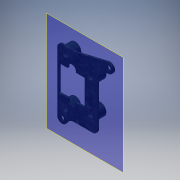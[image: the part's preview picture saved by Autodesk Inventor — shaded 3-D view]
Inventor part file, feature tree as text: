
AUTODESK INVENTOR PART (.ipt)
format: ipt  version: 2017 (Build 210142000, 142)  size: 265,216 bytes
history: native  units: in
note: dims shown in document units (in); Inventor stores cm internally (conversion verified against a paired STEP export)
features: reference x12, other x5, sketch x4, extrude x4, plane x3, fillet x3, projected_geometry x3, chamfer x1
ambient origin geometry x8: Origin, YZ Plane, XZ Plane, XY Plane, X Axis, Y Axis, Z Axis, Center Point
bodies: Solid1 (feature_tree)
feature tree (35):
  sketch  "Sketch1"  dims[d0=1.0in d1=0.0in d2=0.05in d3=0.0in]
  plane  "Work Plane1"
  extrude  "Extrusion1"  Depth=0.05in TaperAngle=0.0deg
  plane  "Work Plane2"
  extrude  "Extrusion2"  Depth=0.2in
  plane  "Work Plane3"
  extrude  "Extrusion3"  Depth=0.05in
  fillet  "Fillet1"  Radius=0.05in
  fillet  "Fillet2"  Radius=0.05in
  fillet  "Fillet3"  Radius=0.05in
  extrude  "Extrusion4"  Depth=0.125in
  chamfer  "Chamfer1"  Distance=0.025in
  reference  "Reference1"
  reference  "Reference2"
  reference  "Reference3"
  reference  "Reference4"
  reference  "Reference5"
  sketch  "Sketch3"  dims[d5=0.2in d6=0.2in]
  reference  "Reference6"
  reference  "Reference7"
  reference  "Reference8"
  sketch  "Sketch4"  dims[d7=0.2in d8=0.2in d15=0.05in d16=0.05in d17=0.05in d18=0.0in]
  projected_geometry  "Projected Loop1"
  projected_geometry  "Projected Loop2"
  projected_geometry  "Projected Loop3"
  reference  "Reference9"
  sketch  "Sketch5"  dims[d19=0.25in d20=0.125in d21=0.025in d22=0.105in d23=0.05in d24=0.0in d25=0.025in d26=0.125in d27=45.0deg]
  reference  "Reference10"
  reference  "Reference11"
  reference  "Reference12"
  other  "<userpath>\Documents\Inventor\PixyCam and Gimbal\Assembly2.iam"
  other  "Assembly2.iam"
  other  "Ring Holder:1"
  other  "frontCase:1"
  other  "Ring Front:1"
